# Revit family: IS_CerathermT50_A7696_BIM_NL
name_source: partatom
category: Plumbing Fixtures
units: mm (PartAtom-declared; Revit-internal decimal feet)

## family parameters
Always vertical = No
Cut with Voids When Loaded = No
OmniClass Number = 23.45.55.17
OmniClass Title = Mixing Faucets
Part Type = Normal
Room Calculation Point = No
Round Connector Dimension = Use Diameter
Shared = No
Work Plane-Based = No

## types (1)
- A7696AA - CERATHERM T50 BATH AND SHOWER THERMOSTATIC EXPOSED OFFSET & KIT  - CHROME
    Accesoires = https://www.idealstandard.nl
    Accessories = https://www.idealstandard.nl
    Afmetingen = 180 x 400 x 325mm
    AfstandsEenheid = Millimeter
    Afwerking = Chrom
    AreaUnits = millimeter
    Artikelnummer = A7696AA
    Artikelomschrijving = CERATHERM T50 BAD- UND DUSCHE THERMOSTAT-OFFSET & KIT
    Artikelreferentie = CERATHERM T50 BAD- UND DUSCHE THERMOSTAT-OFFSET & KIT
    Auteur = Ideal Standard
    BIMObjectName = IS_IdealStandard_ShowerMixers_CerathermT50_A7696
    BIMobject category = Taps & Mixers
    BIMobject category code = sanitary-taps-mixers
    BIMobject main category = Sanitary
    BIMobject main category code = sanitary
    BarCode = 4015413350686
    Bedieningkraan = Drehknopf-Controller
    Bedieningkraanwerk = Drehknopf-Controller
    Beschrijvinggarantie = Herstellergarantie
    BimObjectNaam = IS_IdealStandard_ShowerMixers_CerathermT50_A7696
    Brand = Ideal Standard
    Brand url = http://www.idealstandard.nl
    Breedte = 324.80014
    BrutoGewicht = 0
    Color = Chrom
    ConnectionType = plumbing
    Cost = 0 $
    CurrencyUnit = €
    CurrentRevision = 1
    Date of publishing = 13/08/2021
    Description = CERATHERM T50 BATH AND SHOWER THERMOSTATIC EXPOSED OFFSET & KIT
    Diepte = 181 mm
    Douchebak = No
    DrainSize = 0 mm  [stored 0 ft]
    DurationUnit = Years
    Edition number = 1
    Eigenschappen = T50 BAD UND DUSCHE THERMOSTAT AUSGESETZT UND KIT
    ElementType = Fixed
    FaucetFunction = Shower Mixer
    FaucetOperation = Turning knob controls
    FaucetTopDescription = Turning knob controls
    FaucetType = Shower Mixer
    Features = T50 BAD UND DUSCHE THERMOSTAT AUSGESETZT UND KIT
    Finish = CHROM
    Functieindoucheruimte = Thermostatischer Dusch- und Wannenmischer
    Functiekraanwerk = Thermostatischer Dusch- und Wannenmischer
    GTIN code = https://4015413350686
    Garantieonderdelen = 5
    Garantieunits = Jaren
    Help = https://www.idealstandard.nl
    Hoogte = 401.105079650879
    Hulp = https://www.idealstandard.nl
    IFC Classification = Sanitary Terminal
    IfcExportAs = IfcValveType
    IfcExportType = MIXING
    InletConnectionSize = 0 mm  [stored 0 ft]
    Installatieinstructies = https://www.idealstandard.nl
    Installation instructions = https://www.idealstandard.nl
    InstallationInstructions = https://www.idealstandard.nl
    IsBuiltIn = No
    Klepmechanisme = Thermostatmischer
    Kleur = Chrom
    Lengte = 0 mm  [stored 0 ft]
    LinearUnits = millimeters
    MainColor = Chrome
    MaintenanceInformation = https://www.idealstandard.nl
    Manufacturer = Ideal Standard
    Manufacturer name = Ideal Standard
    ManufacturerURL = http://www.idealstandard.nl
    Masterformat 2014 Code = 22 41 39
    Masterformat 2014 Description = Residential Faucets, Supplies, and Trim
    Materiaal = Messing
    Material = Brass
    Material main = Brass
    MaterialThickness = 0 mm  [stored 0 ft]
    Merk = Ideal Standard
    Model = A7696AA
    ModelNumber = A7696AA
    ModelReference = CERATHERM T50 BATH AND SHOWER THERMOSTATIC EXPOSED OFFSET & KIT
    Montageinstuctie = https://www.idealstandard.nl
    NBS Reference Code = 45-35-70/335
    NBS Reference Description = Shower Mixers
    Name = ShowerMixers_CerathermT50_A7696_IdealStandard
    NettWeight = 340
    Nettogewicht = 340
    NominalDepth = 181 mm
    NominalHeight = 401 mm
    NominalLength = 0 mm  [stored 0 ft]
    NominalWidth = 325 mm
    Normen = ShowerMixers_CerathermT50_A7696_IdealStandard
    OmniClass Code = 23-31 11 15 15
    OmniClass Description = Shower Cartridge Faucets
    OppervlakteEenheid = Millimeter
    Overloop = 0 mm  [stored 0 ft]
    Product Guid = 93010038-1a2e-4a0d-8fe1-592513882c84
    Product SKU = A7696
    Product certification = https://www.idealstandard.nl
    Product data url = https://bimobject.com
    Product family = CERATHERM
    Product group = Shower Mixer
    Product name = CERATHERM T50 BATH AND SHOWER THERMOSTATIC EXPOSED OFFSET & KIT
    Product url = https://www.idealstandard.nl
    ProductInformation = https://www.idealstandard.nl
    Productinformatie = https://www.idealstandard.nl
    QR code = http://bimobject.com
    Referentie = CERATHERM T50 BATH AND SHOWER THERMOSTATIC EXPOSED OFFSET & KIT
    Revisie = 1
    Shape = cylindrical
    ShowerType = thermostatic shower mixer
    Size = 180 x 400 x 325mm
    Space = Internal
    SpareParts = https://www.idealstandard.nl
    Technical description = https://www.idealstandard.nl
    Telefoonnummer = (0228) 521-580
    TestPressure = 10  bar
    Testdruk = 10 bar
    UNSPSC Code = 301815
    URL = http://www.idealstandard.nl
    Uniclass 1.4 Code = L725111
    Uniclass 1.4 Description = Mixer taps
    Uniclass 2.0 Code = PR-35-06-82
    Uniclass 2.0 Description = Shower Mixers
    Uniclass 2015 Code = Pr_40_20_87_78
    Uniclass 2015 Name = Shower manual water supply sets
    Uniclass2015Beschrijving = Shower manual water supply sets
    Uniclass2015Code = Pr_40_20_87_78
    Uniclass2015Referentie = Pr_40_20_87_78
    Uniclass2015Title = Shower manual water supply sets
    Uniclass2015Version = v1.22
    Urlproducent = http://www.idealstandard.nl
    ValutaEenheid = €
    ValveOperation = thermostatic
    Versie = 1
    Version = 1
    Vervangingskosten = 0
    VolumeUnits = Liters
    Volumeunits = Liter
    Vorm = Zylindrisch
    WRASURL = https://www.wrasapprovals.co.uk
    WarrantyDescription = manufacturer warranty
    WarrantyDurationParts = 5
    WarrantyDurationUnit = years
    Wisselstukken = https://www.idealstandard.nl
    Youtube clip = https://www.youtube.com

note: [stored X ft] marks values corroborated as IEEE doubles in the binary element streams (Revit-internal decimal feet)

## geometry (parser evidence)
native form markers: Sweep x2
no freeform markers — native parametric forms only
